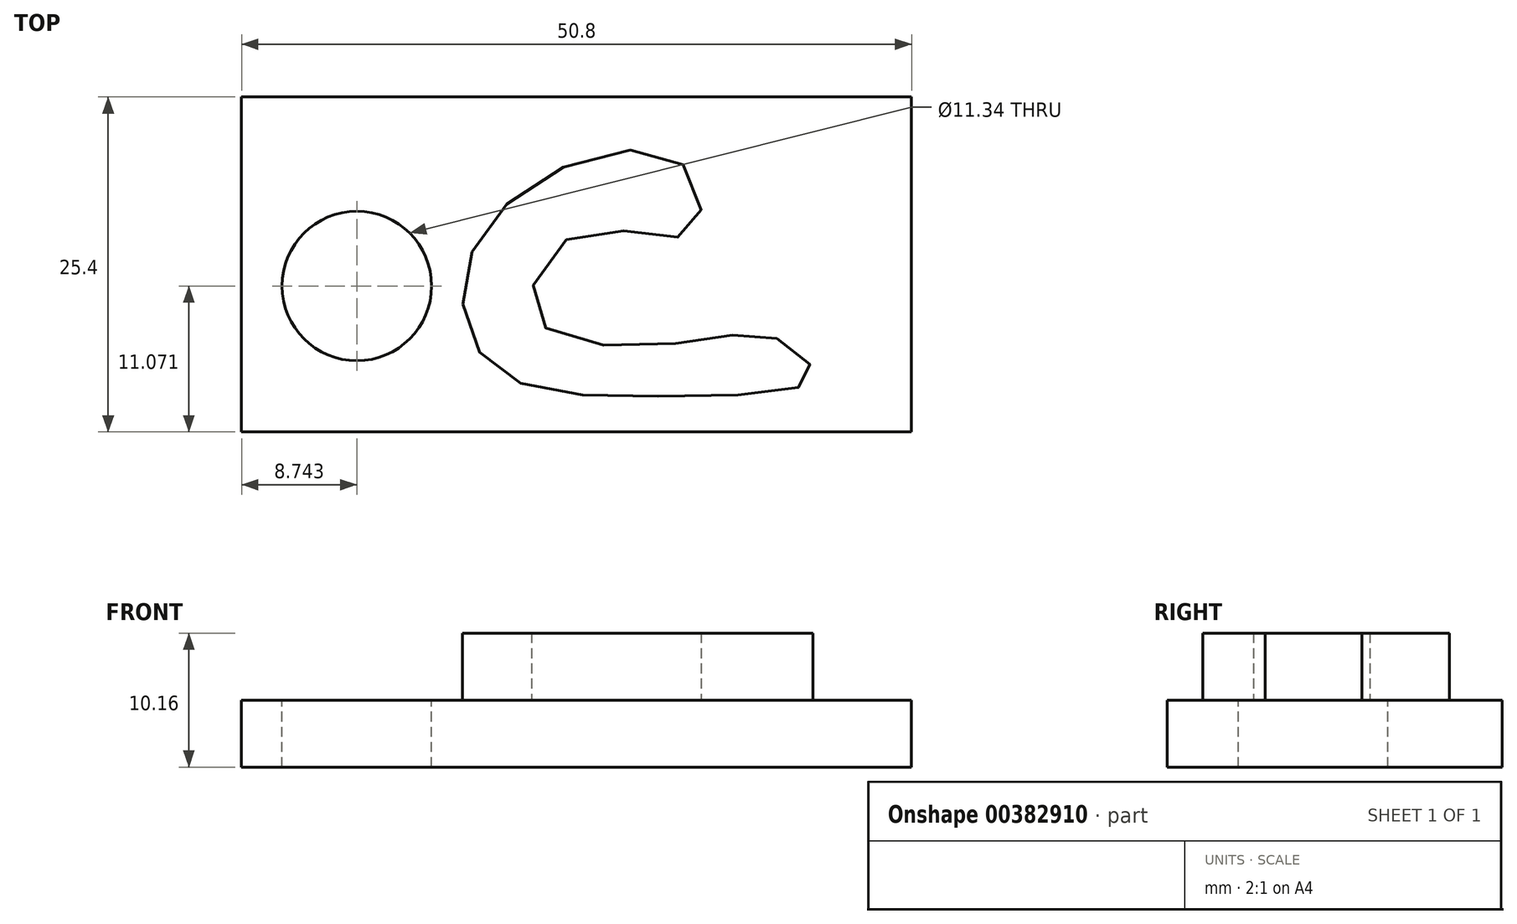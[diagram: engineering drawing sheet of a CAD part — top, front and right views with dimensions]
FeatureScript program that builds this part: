
annotation { "Feature Type Name" : "Feature", "Feature Type Description" : "" }
export const myFeature = defineFeature(function(context is Context, id is Id, definition is map)
    precondition{}
    {
        {
            var Q0;
            Q0=qCreatedBy(makeId("Top.planeOp"),FACE);
            var sketch = newSketch(context, id + "F0", { "sketchPlane" : qUnion([Q0])});
            skLineSegment(sketch, "E0.bottom", {"start": v(-36.66, 10.3) * mm, "end": v(14.14, 10.3) * mm});
            skLineSegment(sketch, "E0.top", {"start": v(-36.66, -15.1) * mm, "end": v(14.14, -15.1) * mm});
            skLineSegment(sketch, "E0.left", {"start": v(-36.66, 10.3) * mm, "end": v(-36.66, -15.1) * mm});
            skLineSegment(sketch, "E0.right", {"start": v(14.14, 10.3) * mm, "end": v(14.14, -15.1) * mm});
            skSolve(sketch);
        }
        {
            var Q0;
            Q0=makeQuery(id+"F0.imprint","IMPRINT",FACE,{"disambiguationData":[TD([[makeQuery(id+"F0.imprint","IMPRINT",EDGE,{"derivedFrom":sQuery(id+"F0.wireOp",EDGE,"E0.bottom")}),-1.0]])]});
            extrude(context, id + "F1", {"entities" : qUnion([Q0]), "depth" : 5.08 * mm});
        }
        {
            var Q0;
            Q0=makeQuery(id+"F1.opExtrude","CAP_FACE",FACE,{"disambiguationData":[OSD([sQuery(id+"F0.wireOp",EDGE,"E0.bottom"),sQuery(id+"F0.wireOp",EDGE,"E0.top"),sQuery(id+"F0.wireOp",EDGE,"E0.left"),sQuery(id+"F0.wireOp",EDGE,"E0.right")])],"isStart":false});
            var sketch = newSketch(context, id + "F2", { "sketchPlane" : qUnion([Q0])});
            skCircle(sketch, "E1", {"center": v(-31.66, -2.3) * mm, "radius": 3.48 * mm});
            skFitSpline(sketch, "E2", {"points": [v(-3.17, 5.18) * mm, v(-14.1, 4.03) * mm, v(-19.86, -4.03) * mm, v(-16.98, -10.65) * mm, v(-3.74, -12.38) * mm, v(6.62, -10.94) * mm, v(4.03, -8.06) * mm, v(-3.45, -8.35) * mm, v(-14.4, -6.33) * mm, v(-10.94, 0) * mm, v(-2.6, 0) * mm, v(-3.17, 5.18) * mm]});
            skSolve(sketch);
        }
        {
            var Q0;
            Q0=makeQuery(id+"F2.imprint","IMPRINT",FACE,{"disambiguationData":[TD([[makeQuery(id+"F2.imprint","IMPRINT",EDGE,{"derivedFrom":sQuery(id+"F2.wireOp",EDGE,"E2")}),1.0]])]});
            extrude(context, id + "F3", {"entities" : qUnion([Q0]), "operationType" : NewBodyOperationType.ADD, "depth" : 5.08 * mm});
        }
        {
            var Q0;
            Q0=makeQuery(id+"F1.opExtrude","CAP_FACE",FACE,{"disambiguationData":[OSD([sQuery(id+"F0.wireOp",EDGE,"E0.bottom"),sQuery(id+"F0.wireOp",EDGE,"E0.top"),sQuery(id+"F0.wireOp",EDGE,"E0.left"),sQuery(id+"F0.wireOp",EDGE,"E0.right")])],"isStart":false});
            var sketch = newSketch(context, id + "F4", { "sketchPlane" : qUnion([Q0])});
            skCircle(sketch, "E3", {"center": v(-27.92, -4.03) * mm, "radius": 5.67 * mm});
            skSolve(sketch);
        }
        {
            var Q0;
            Q0=makeQuery(id+"F4.imprint","IMPRINT",FACE,{"disambiguationData":[TD([[makeQuery(id+"F4.imprint","IMPRINT",EDGE,{"derivedFrom":sQuery(id+"F4.wireOp",EDGE,"E3")}),1.0]])]});
            extrude(context, id + "F5", {"entities" : qUnion([Q0]), "operationType" : NewBodyOperationType.REMOVE, "oppositeDirection" : true, "depth" : 25.4 * mm});
        }
    });
